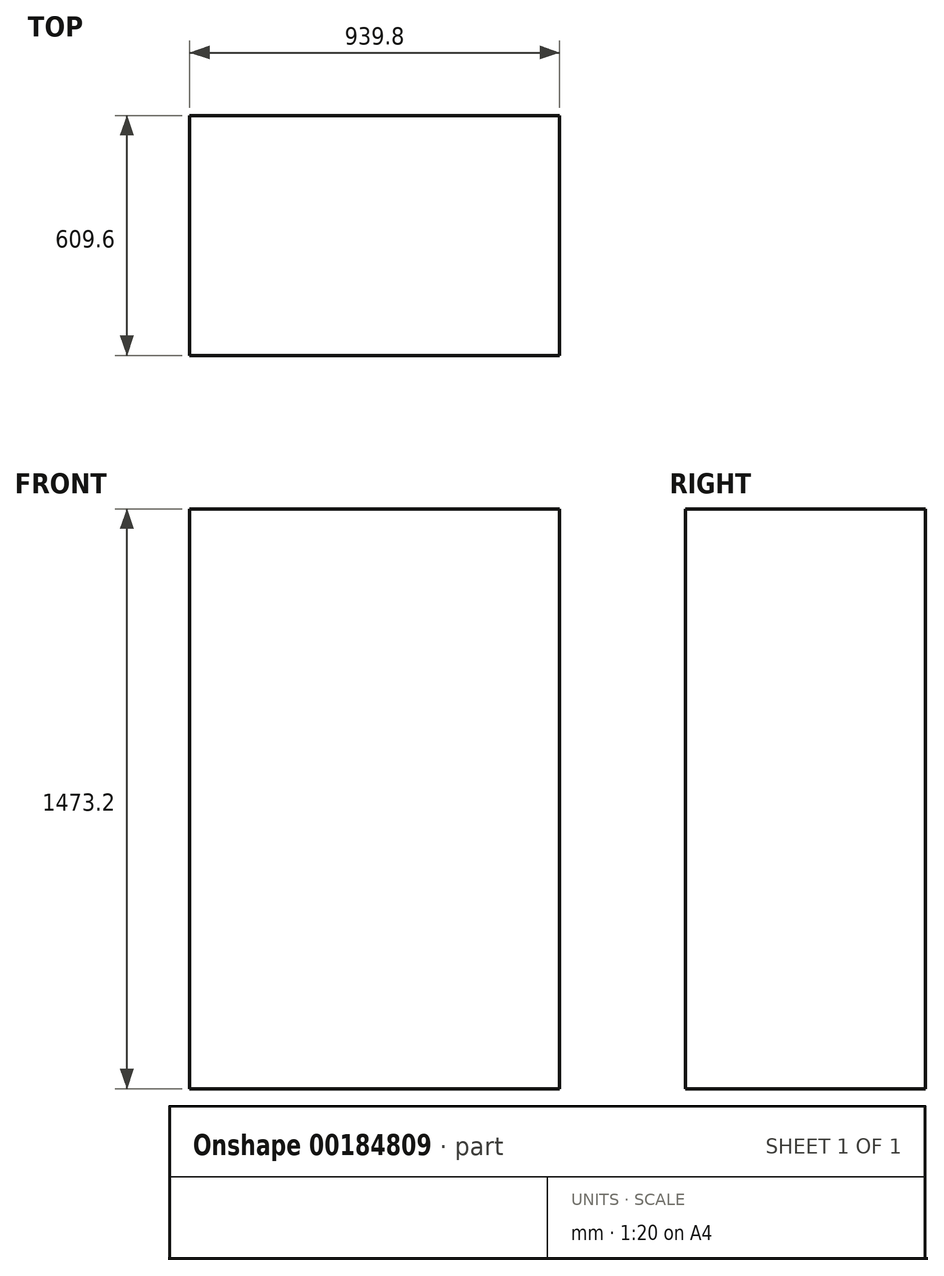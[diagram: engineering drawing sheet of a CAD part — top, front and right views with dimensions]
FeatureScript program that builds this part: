
annotation { "Feature Type Name" : "Feature", "Feature Type Description" : "" }
export const myFeature = defineFeature(function(context is Context, id is Id, definition is map)
    precondition{}
    {
        {
            var Q0;
            Q0=qCreatedBy(makeId("Top.planeOp"),FACE);
            var sketch = newSketch(context, id + "F0", { "sketchPlane" : qUnion([Q0])});
            skLineSegment(sketch, "E0.bottom", {"start": v(469.9, -304.8) * mm, "end": v(-469.9, -304.8) * mm});
            skLineSegment(sketch, "E0.top", {"start": v(469.9, 304.8) * mm, "end": v(-469.9, 304.8) * mm});
            skLineSegment(sketch, "E0.left", {"start": v(469.9, -304.8) * mm, "end": v(469.9, 304.8) * mm});
            skLineSegment(sketch, "E0.right", {"start": v(-469.9, -304.8) * mm, "end": v(-469.9, 304.8) * mm});
            skPoint(sketch, "E0.middle", {"position": v(0, 0) * mm});
            skSolve(sketch);
        }
        {
            var Q0;
            Q0 = qSketchRegion(id + "F0", true);
            extrude(context, id + "F1", {"entities" : qUnion([Q0]), "depth" : 1473.2 * mm});
        }
    });
